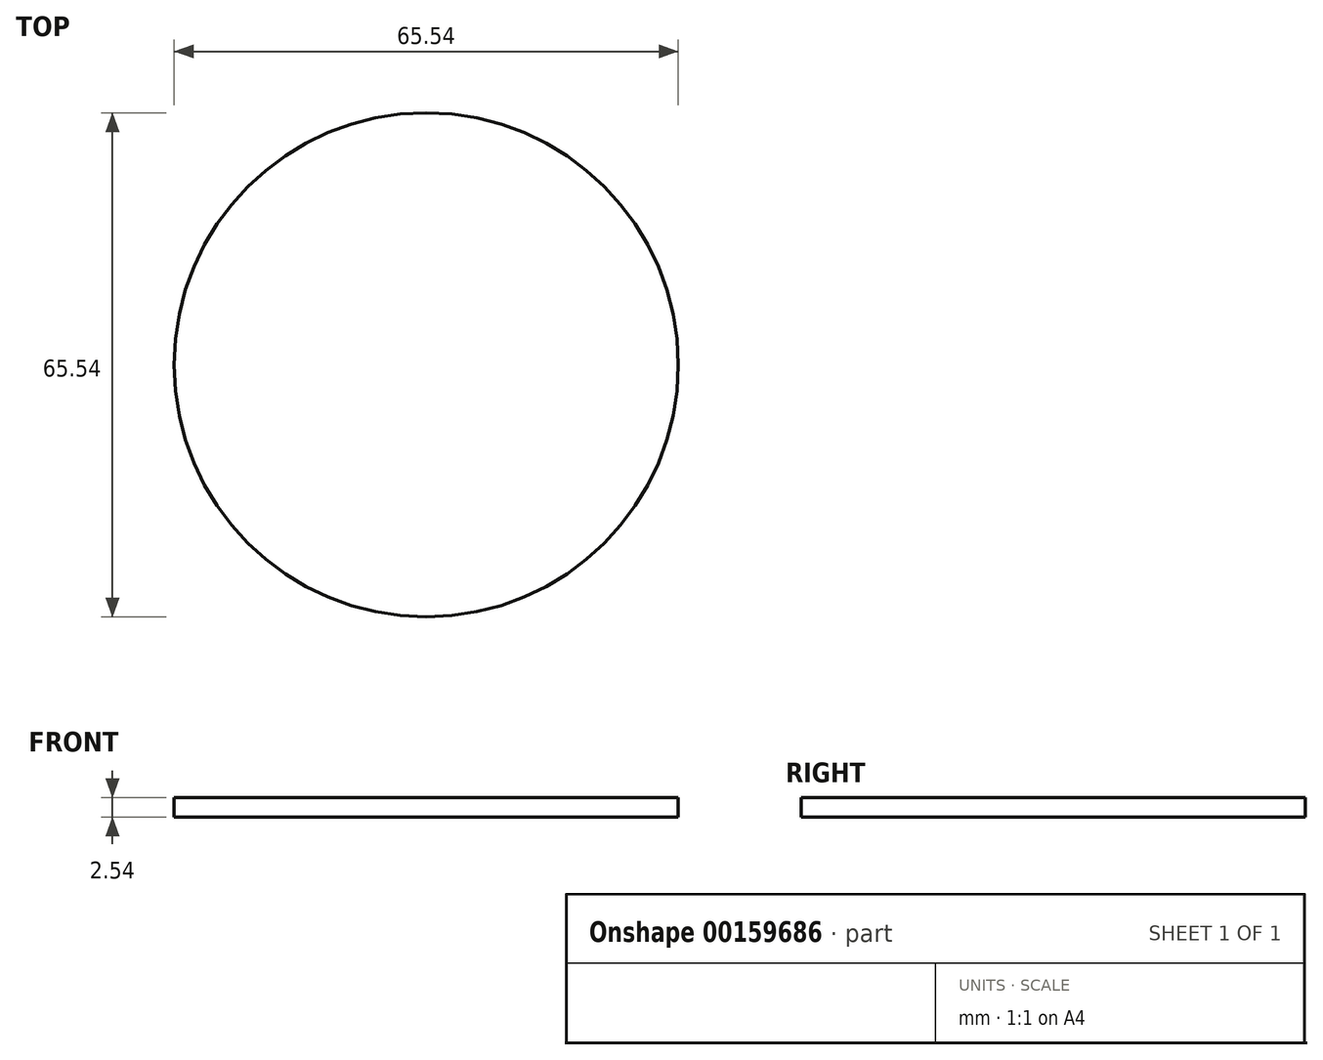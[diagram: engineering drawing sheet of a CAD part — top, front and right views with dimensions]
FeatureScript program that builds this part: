
annotation { "Feature Type Name" : "Feature", "Feature Type Description" : "" }
export const myFeature = defineFeature(function(context is Context, id is Id, definition is map)
    precondition{}
    {
        {
            var Q0;
            Q0=qCreatedBy(makeId("Top.planeOp"),FACE);
            var sketch = newSketch(context, id + "F0", { "sketchPlane" : qUnion([Q0])});
            skCircle(sketch, "E0", {"center": v(0, 0) * mm, "radius": 39.12 * mm});
            skSolve(sketch);
        }
        {
            var Q0;
            Q0=makeQuery(id+"F0.imprint","IMPRINT",FACE,{"disambiguationData":[TD([[makeQuery(id+"F0.imprint","IMPRINT",EDGE,{"derivedFrom":sQuery(id+"F0.wireOp",EDGE,"E0")}),1.0]])]});
            extrude(context, id + "F1", {"entities" : qUnion([Q0]), "depth" : 25.4 * mm});
        }
        {
            var Q0;
            Q0=makeQuery(id+"F1.opExtrude","CAP_FACE",FACE,{"disambiguationData":[OSD([sQuery(id+"F0.wireOp",EDGE,"E0")])],"isStart":false});
            shell(context, id + "F2", {"entities" : qUnion([Q0]), "thickness" : 2.54 * mm});
        }
        {
            var Q0;
            Q0=makeQuery(id+"F1.opExtrude","CAP_FACE",FACE,{"disambiguationData":[OSD([sQuery(id+"F0.wireOp",EDGE,"E0")])],"isStart":true});
            var sketch = newSketch(context, id + "F3", { "sketchPlane" : qUnion([Q0])});
            skCircle(sketch, "E1.0", {"center": v(0, 0) * mm, "radius": 32.77 * mm});
            skSolve(sketch);
        }
        {
            var Q0;
            Q0=makeQuery(id+"F3.imprint","IMPRINT",FACE,{"disambiguationData":[TD([[makeQuery(id+"F3.imprint","IMPRINT",EDGE,{"derivedFrom":sQuery(id+"F3.wireOp",EDGE,"E1.0")}),-1.0]])]});
            extrude(context, id + "F4", {"entities" : qUnion([Q0]), "operationType" : NewBodyOperationType.REMOVE, "oppositeDirection" : true, "depth" : 25.4 * mm});
        }
    });
